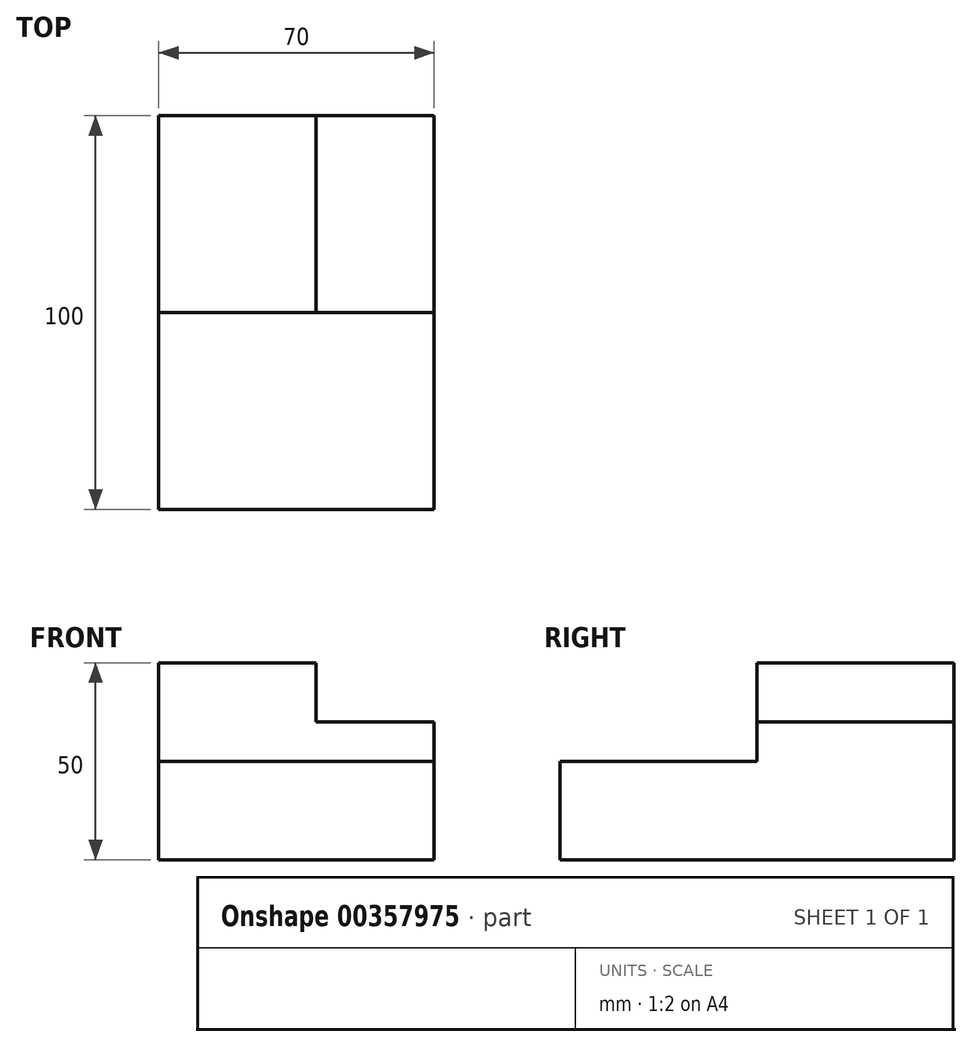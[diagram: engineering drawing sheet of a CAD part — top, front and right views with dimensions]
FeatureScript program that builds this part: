
annotation { "Feature Type Name" : "Feature", "Feature Type Description" : "" }
export const myFeature = defineFeature(function(context is Context, id is Id, definition is map)
    precondition{}
    {
        {
            var Q0;
            Q0=qCreatedBy(makeId("Top.planeOp"),FACE);
            var sketch = newSketch(context, id + "F0", { "sketchPlane" : qUnion([Q0])});
            skLineSegment(sketch, "E0.bottom", {"start": v(-35, 50) * mm, "end": v(35, 50) * mm});
            skLineSegment(sketch, "E0.top", {"start": v(-35, -50) * mm, "end": v(35, -50) * mm});
            skLineSegment(sketch, "E0.left", {"start": v(-35, 50) * mm, "end": v(-35, -50) * mm});
            skLineSegment(sketch, "E0.right", {"start": v(35, 50) * mm, "end": v(35, -50) * mm});
            skPoint(sketch, "E0.middle", {"position": v(0, 0) * mm});
            skSolve(sketch);
        }
        {
            var Q0;
            Q0 = qSketchRegion(id + "F0", true);
            extrude(context, id + "F1", {"entities" : qUnion([Q0]), "depth" : 50 * mm});
        }
        {
            var Q0;
            Q0=makeQuery(id+"F1.opExtrude","CAP_FACE",FACE,{"disambiguationData":[OSD([sQuery(id+"F0.wireOp",EDGE,"E0.bottom"),sQuery(id+"F0.wireOp",EDGE,"E0.top"),sQuery(id+"F0.wireOp",EDGE,"E0.left"),sQuery(id+"F0.wireOp",EDGE,"E0.right")])],"isStart":false});
            var sketch = newSketch(context, id + "F2", { "sketchPlane" : qUnion([Q0])});
            skLineSegment(sketch, "E1.bottom", {"start": v(35, -50) * mm, "end": v(-35, -50) * mm});
            skLineSegment(sketch, "E1.top", {"start": v(35, 0) * mm, "end": v(-35, 0) * mm});
            skLineSegment(sketch, "E1.left", {"start": v(35, -50) * mm, "end": v(35, 0) * mm});
            skLineSegment(sketch, "E1.right", {"start": v(-35, -50) * mm, "end": v(-35, 0) * mm});
            skSolve(sketch);
        }
        {
            var Q0;
            Q0 = qSketchRegion(id + "F2", true);
            extrude(context, id + "F3", {"entities" : qUnion([Q0]), "operationType" : NewBodyOperationType.REMOVE, "oppositeDirection" : true, "depth" : 25 * mm});
        }
        {
            var Q0;
            Q0=makeQuery(id+"F1.opExtrude","CAP_FACE",FACE,{"disambiguationData":[OSD([sQuery(id+"F0.wireOp",EDGE,"E0.bottom"),sQuery(id+"F0.wireOp",EDGE,"E0.top"),sQuery(id+"F0.wireOp",EDGE,"E0.left"),sQuery(id+"F0.wireOp",EDGE,"E0.right")])],"isStart":false});
            var sketch = newSketch(context, id + "F4", { "sketchPlane" : qUnion([Q0])});
            skLineSegment(sketch, "E2.bottom", {"start": v(35, 50) * mm, "end": v(5, 50) * mm});
            skLineSegment(sketch, "E2.top", {"start": v(35, 0) * mm, "end": v(5, 0) * mm});
            skLineSegment(sketch, "E2.left", {"start": v(35, 50) * mm, "end": v(35, 0) * mm});
            skLineSegment(sketch, "E2.right", {"start": v(5, 50) * mm, "end": v(5, 0) * mm});
            skSolve(sketch);
        }
        {
            var Q0;
            Q0 = qSketchRegion(id + "F4", true);
            var Q1;
            Q1=makeQuery(id+"F3.boolean.opBoolean","COPY",FACE,{"derivedFrom":makeQuery(id+"F3.opExtrude","CAP_FACE",FACE,{"disambiguationData":[OSD([sQuery(id+"F2.wireOp",EDGE,"E1.bottom"),sQuery(id+"F2.wireOp",EDGE,"E1.top"),sQuery(id+"F2.wireOp",EDGE,"E1.left"),sQuery(id+"F2.wireOp",EDGE,"E1.right")])],"isStart":false})});
            extrude(context, id + "F5", {"entities" : qUnion([Q0]), "operationType" : NewBodyOperationType.REMOVE, "oppositeDirection" : true, "endBoundEntityFace" : qUnion([Q1]), "depth" : 15 * mm});
        }
    });
